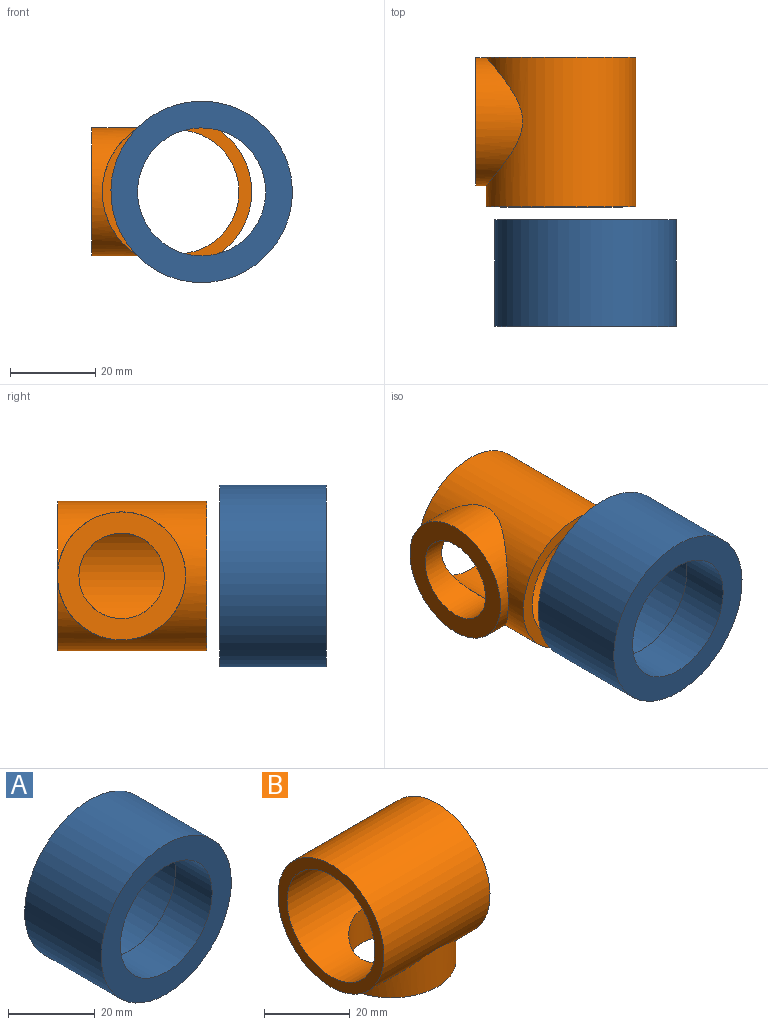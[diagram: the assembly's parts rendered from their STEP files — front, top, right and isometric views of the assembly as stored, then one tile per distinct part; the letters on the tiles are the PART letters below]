
ASSEMBLY  parts=2 mates=1
PART A: 6 faces, bbox 42.5x25x42.5 mm
  f0: cylinder r=17mm len=34mm, axis (0,1,0), area 1388.6mm2, adj f3,f5
  f1: cylinder r=21.25mm len=42.5mm, axis (0,1,0), area 3337.9mm2, adj f2,f3
  f2: plane 42.5x42.5mm, normal (0,-1,0), area 711.8mm2, adj f1,f4
  f3: plane 42.5x42.5mm, normal (0,1,0), area 510.7mm2, adj f0,f1
  f4: cylinder r=15mm len=30mm, axis (0,-1,0), area 1131mm2, adj f2,f5
  f5: plane 34x34mm, normal (0,1,0), area 201.1mm2, adj f0,f4
PART B: 7 faces, bbox 35x35x37.5 mm
  f0: cylinder r=17.5mm len=35mm, axis (-1,0,0), area 3045.7mm2, adj f2,f5,f6
  f1: cylinder r=14.5mm len=35mm, axis (-1,0,0), area 2851.4mm2, adj f2,f3,f6
  f2: plane 35x35mm, normal (-1,0,0), area 301.6mm2, adj f0,f1
  f3: cylinder r=10mm len=20mm, axis (0,0,1), area 466.2mm2, adj f1,f4
  f4: plane 30x30mm, normal (0,0,-1), area 392.7mm2, adj f3,f5
  f5: cylinder r=15mm len=30mm, axis (0,0,-1), area 603.2mm2, adj f0,f4
  f6: plane 35x35mm, normal (1,0,0), area 301.6mm2, adj f0,f1
PLACE A t=(7.31,25.25,12.79)mm
PLACE B rot(axis=(0.58,0.58,0.58),120deg) t=(1.56,28.25,12.79)mm
MATE parallel B.f0 <-> A.f1  axis (0,-1,0) through (1.56,28.25,12.79)mm
